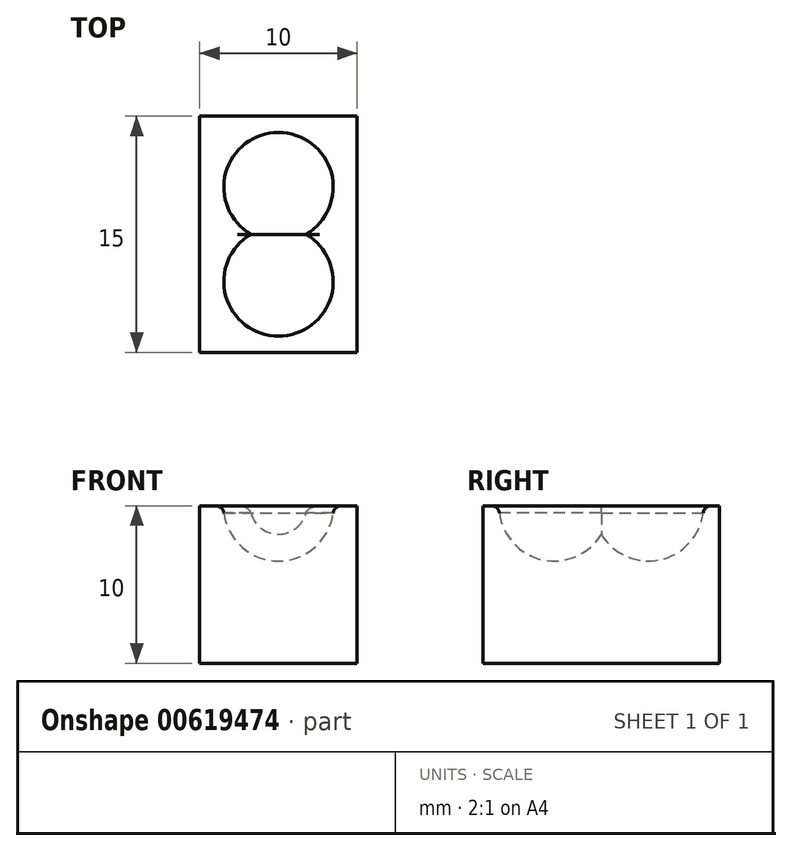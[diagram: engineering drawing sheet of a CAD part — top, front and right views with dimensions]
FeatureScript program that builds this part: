
annotation { "Feature Type Name" : "Feature", "Feature Type Description" : "" }
export const myFeature = defineFeature(function(context is Context, id is Id, definition is map)
    precondition{}
    {
        {
            var Q0;
            Q0=qCreatedBy(makeId("Top.planeOp"),FACE);
            var sketch = newSketch(context, id + "F0", { "sketchPlane" : qUnion([Q0])});
            skLineSegment(sketch, "E0.bottom", {"start": v(-5, 7.5) * mm, "end": v(5, 7.5) * mm});
            skLineSegment(sketch, "E0.top", {"start": v(-5, -7.5) * mm, "end": v(5, -7.5) * mm});
            skLineSegment(sketch, "E0.left", {"start": v(-5, 7.5) * mm, "end": v(-5, -7.5) * mm});
            skLineSegment(sketch, "E0.right", {"start": v(5, 7.5) * mm, "end": v(5, -7.5) * mm});
            skSolve(sketch);
        }
        {
            var Q0;
            Q0=makeQuery(id+"F0.imprint","IMPRINT",FACE,{"disambiguationData":[TD([[makeQuery(id+"F0.imprint","IMPRINT",EDGE,{"derivedFrom":sQuery(id+"F0.wireOp",EDGE,"E0.bottom")}),-1.0]])]});
            extrude(context, id + "F1", {"entities" : qUnion([Q0]), "oppositeDirection" : true, "depth" : 10 * mm, "offsetDistance" : 25 * mm});
        }
        {
            var Q0;
            Q0=makeQuery(id+"F1.opExtrude","CAP_FACE",FACE,{"disambiguationData":[OSD([sQuery(id+"F0.wireOp",EDGE,"E0.bottom"),sQuery(id+"F0.wireOp",EDGE,"E0.top"),sQuery(id+"F0.wireOp",EDGE,"E0.left"),sQuery(id+"F0.wireOp",EDGE,"E0.right")])],"isStart":true});
            var sketch = newSketch(context, id + "F2", { "sketchPlane" : qUnion([Q0])});
            skLineSegment(sketch, "E1", {"start": v(0, 9.2) * mm, "end": v(0, -8.76) * mm});
            skArc(sketch, "E2", {"start": v(0, -0.5) * mm, "mid": v(3.5, 3) * mm, "end": v(0, 6.5) * mm});
            skArc(sketch, "E3", {"start": v(0, -6.5) * mm, "mid": v(3.5, -3) * mm, "end": v(0, 0.5) * mm});
            skPoint(sketch, "E4", {"position": v(0, 0.22) * mm});
            skSolve(sketch);
        }
        {
            var Q0;
            Q0 = qSketchRegion(id + "F2", true);
            var Q1;
            Q1=sQuery(id+"F2.wireOp",EDGE,"E1");
            revolve(context, id + "F3", {"operationType" : NewBodyOperationType.REMOVE, "entities" : qUnion([Q0]), "axis" : qUnion([Q1]), "revolveType" : RevolveType.FULL, "oppositeDirection" : true});
        }
        {
            var Q0;
            Q0=makeQuery(id+"F3.boolean.opBoolean","INTERSECT",EDGE,{"derivedFrom":[makeQuery(id+"F1.opExtrude","CAP_FACE",FACE,{"disambiguationData":[OSD([sQuery(id+"F0.wireOp",EDGE,"E0.bottom"),sQuery(id+"F0.wireOp",EDGE,"E0.top"),sQuery(id+"F0.wireOp",EDGE,"E0.left"),sQuery(id+"F0.wireOp",EDGE,"E0.right")])],"isStart":true}),makeQuery(id+"F3.opRevolve","SWEPT_FACE",FACE,{"disambiguationData":[OSD([sQuery(id+"F2.wireOp",EDGE,"E2")])]})]});
            var Q1;
            Q1=makeQuery(id+"F3.boolean.opBoolean","INTERSECT",EDGE,{"derivedFrom":[makeQuery(id+"F1.opExtrude","CAP_FACE",FACE,{"disambiguationData":[OSD([sQuery(id+"F0.wireOp",EDGE,"E0.bottom"),sQuery(id+"F0.wireOp",EDGE,"E0.top"),sQuery(id+"F0.wireOp",EDGE,"E0.left"),sQuery(id+"F0.wireOp",EDGE,"E0.right")])],"isStart":true}),makeQuery(id+"F3.opRevolve","SWEPT_FACE",FACE,{"disambiguationData":[OSD([sQuery(id+"F2.wireOp",EDGE,"E3")])]})]});
            fillet(context, id + "F4", {"entities" : qUnion([Q0, Q1]), "radius" : .5 * mm, "tangentPropagation" : true, "allowEdgeOverflow" : false});
        }
    });
